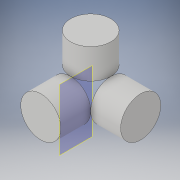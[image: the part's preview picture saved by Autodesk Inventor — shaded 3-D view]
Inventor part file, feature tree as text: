
AUTODESK INVENTOR PART (.ipt)
format: ipt  version: 2018 (Build 220112000, 112)  size: 142,848 bytes
history: native  units: in
note: dims shown in document units (in); Inventor stores cm internally (conversion verified against a paired STEP export)
features: sketch x6, plane x4, extrude x3, revolve x3
ambient origin geometry x8: Origin, YZ Plane, XZ Plane, XY Plane, X Axis, Y Axis, Z Axis, Center Point
bodies: Body1 (feature_tree)
feature tree (16):
  extrude  "Extrusion7"  Depth=1.198in TaperAngle=0.0deg
  sketch  "Sketch12"  dims[d33=90.0deg d34=2.0in]
  plane  "Work Plane4"
  sketch  "Sketch13"  dims[d35=1.605in d36=2.0in]
  sketch  "Sketch14"  dims[d37=1.197in d38=0.0in d39=90.0deg]
  plane  "Work Plane5"
  extrude  "Extrusion8"  Depth=2.0in
  plane  "Work Plane6"
  sketch  "Sketch15"  dims[d40=2.0in d41=1.605in]
  plane  "Work Plane7"
  extrude  "Extrusion9"  Depth=2.0in
  sketch  "Sketch16"  dims[d42=2.0in d43=1.197in d44=0.0in d45=90.0deg d48=90.0deg d49=90.0deg]
  revolve  "Revolution11"  Angle=90.0deg
  revolve  "Revolution7"  [1 undecoded]
  revolve  "Revolution10"  [1 undecoded]
  sketch  "Sketch11"  dims[d30=1.605in d31=1.198in d32=0.0in]
note: 2 required parameter values undecoded (feature->parameter linkage not recoverable at this tier; creation-order binding heuristic only, values carry confidence <= 0.55)
